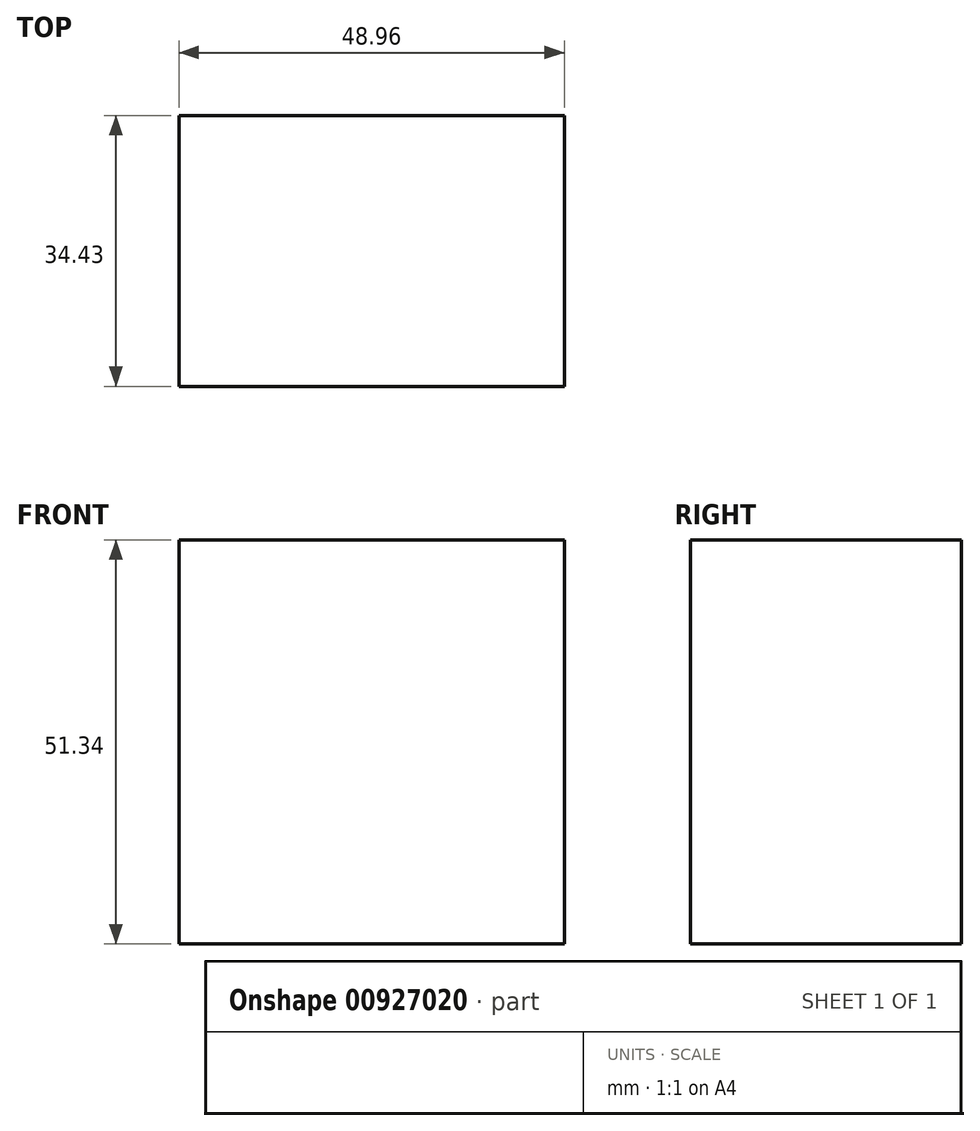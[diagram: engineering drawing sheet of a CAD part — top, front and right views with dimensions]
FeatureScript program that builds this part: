
annotation { "Feature Type Name" : "Feature", "Feature Type Description" : "" }
export const myFeature = defineFeature(function(context is Context, id is Id, definition is map)
    precondition{}
    {
        {
            var Q0;
            Q0=qCreatedBy(makeId("Top.planeOp"),FACE);
            var sketch = newSketch(context, id + "F0", { "sketchPlane" : qUnion([Q0])});
            skLineSegment(sketch, "E0.bottom", {"start": v(-34.85, -39.62) * mm, "end": v(-27.38, -39.62) * mm});
            skLineSegment(sketch, "E0.top", {"start": v(-34.85, -17.22) * mm, "end": v(-27.38, -17.22) * mm});
            skLineSegment(sketch, "E0.left", {"start": v(-34.85, -39.62) * mm, "end": v(-34.85, -17.22) * mm});
            skLineSegment(sketch, "E0.right", {"start": v(-27.38, -39.62) * mm, "end": v(-27.38, -17.22) * mm});
            skPoint(sketch, "E0.middle", {"position": v(-31.12, -28.42) * mm});
            skLineSegment(sketch, "E1.bottom", {"start": v(0, -22.4) * mm, "end": v(48.96, -22.4) * mm});
            skLineSegment(sketch, "E1.top", {"start": v(0, -56.84) * mm, "end": v(48.96, -56.84) * mm});
            skLineSegment(sketch, "E1.left", {"start": v(0, -22.4) * mm, "end": v(0, -56.84) * mm});
            skLineSegment(sketch, "E1.right", {"start": v(48.96, -22.4) * mm, "end": v(48.96, -56.84) * mm});
            skPoint(sketch, "E1.middle", {"position": v(24.48, -39.62) * mm});
            skLineSegment(sketch, "E2.bottom", {"start": v(-31.12, -28.42) * mm, "end": v(-23.65, -28.42) * mm});
            skLineSegment(sketch, "E2.top", {"start": v(-31.12, -50.83) * mm, "end": v(-23.65, -50.83) * mm});
            skLineSegment(sketch, "E2.left", {"start": v(-31.12, -28.42) * mm, "end": v(-31.12, -50.83) * mm});
            skLineSegment(sketch, "E2.right", {"start": v(-23.65, -28.42) * mm, "end": v(-23.65, -50.83) * mm});
            skPoint(sketch, "E2.middle", {"position": v(-27.38, -39.62) * mm});
            skSolve(sketch);
        }
        {
            var Q0;
            Q0=makeQuery(id+"F0.imprint","IMPRINT",FACE,{"disambiguationData":[TD([[makeQuery(id+"F0.imprint","IMPRINT",EDGE,{"derivedFrom":sQuery(id+"F0.wireOp",EDGE,"E1.bottom")}),-1.0]])]});
            extrude(context, id + "F1", {"entities" : qUnion([Q0]), "depth" : 51.34 * mm, "offsetDistance" : 25.4 * mm});
        }
    });
